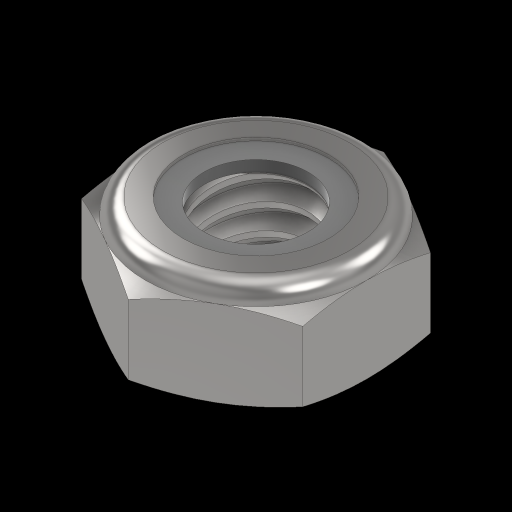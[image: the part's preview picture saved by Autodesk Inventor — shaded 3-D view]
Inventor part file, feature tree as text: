
AUTODESK INVENTOR PART (.ipt)
format: ipt  version: 2024.2 (Build 282272000, 272)  size: 283,648 bytes
history: native  units: in
note: dims shown in document units (in); Inventor stores cm internally (conversion verified against a paired STEP export)
features: other x1, revolve x1
ambient origin geometry x8: Origin, YZ Plane, XZ Plane, XY Plane, X Axis, Y Axis, Z Axis, Center Point
bodies: Solid1 (feature_tree), Solid2 (feature_tree)
feature tree (2):
  other  "Cut-Revolve4"
  revolve  "Revolve2"  [1 undecoded]
note: 1 required parameter value undecoded (feature->parameter linkage not recoverable at this tier; creation-order binding heuristic only, values carry confidence <= 0.55)
